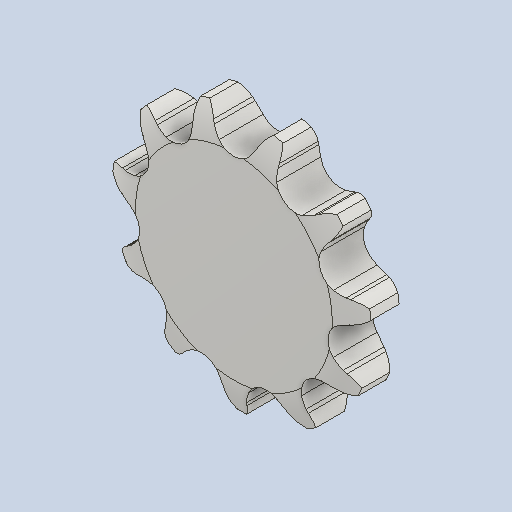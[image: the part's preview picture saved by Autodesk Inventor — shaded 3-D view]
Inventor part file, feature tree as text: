
AUTODESK INVENTOR PART (.ipt)
format: ipt  version: 2022.1 (Build 261234000, 234)  size: 422,912 bytes
history: native  units: mm
features: other x6, extrude x2, pattern_linear x1, pattern_circular x1
ambient origin geometry x8: Origin, YZ Plane, XZ Plane, XY Plane, X Axis, Y Axis, Z Axis, Center Point
bodies: Solid1 (feature_tree)
feature tree (10):
  other  "Perfil de diente teórico"
  other  "Perfil de diente"
  other  "Perfil de sección"
  other  "Cubierta"
  other  "Ramal"
  pattern_linear  "Patrón de ramal"  Spacing1=88.736638mm  [1 undecoded]
  extrude  "Diente teórico"  Depth=5.711987mm
  extrude  "Diente"  Depth=7.575mm
  pattern_circular  "Patrón de diente"  [2 undecoded]
  other  "Plano síncrono"
note: 3 required parameter values undecoded (feature->parameter linkage not recoverable at this tier; creation-order binding heuristic only, values carry confidence <= 0.55)
